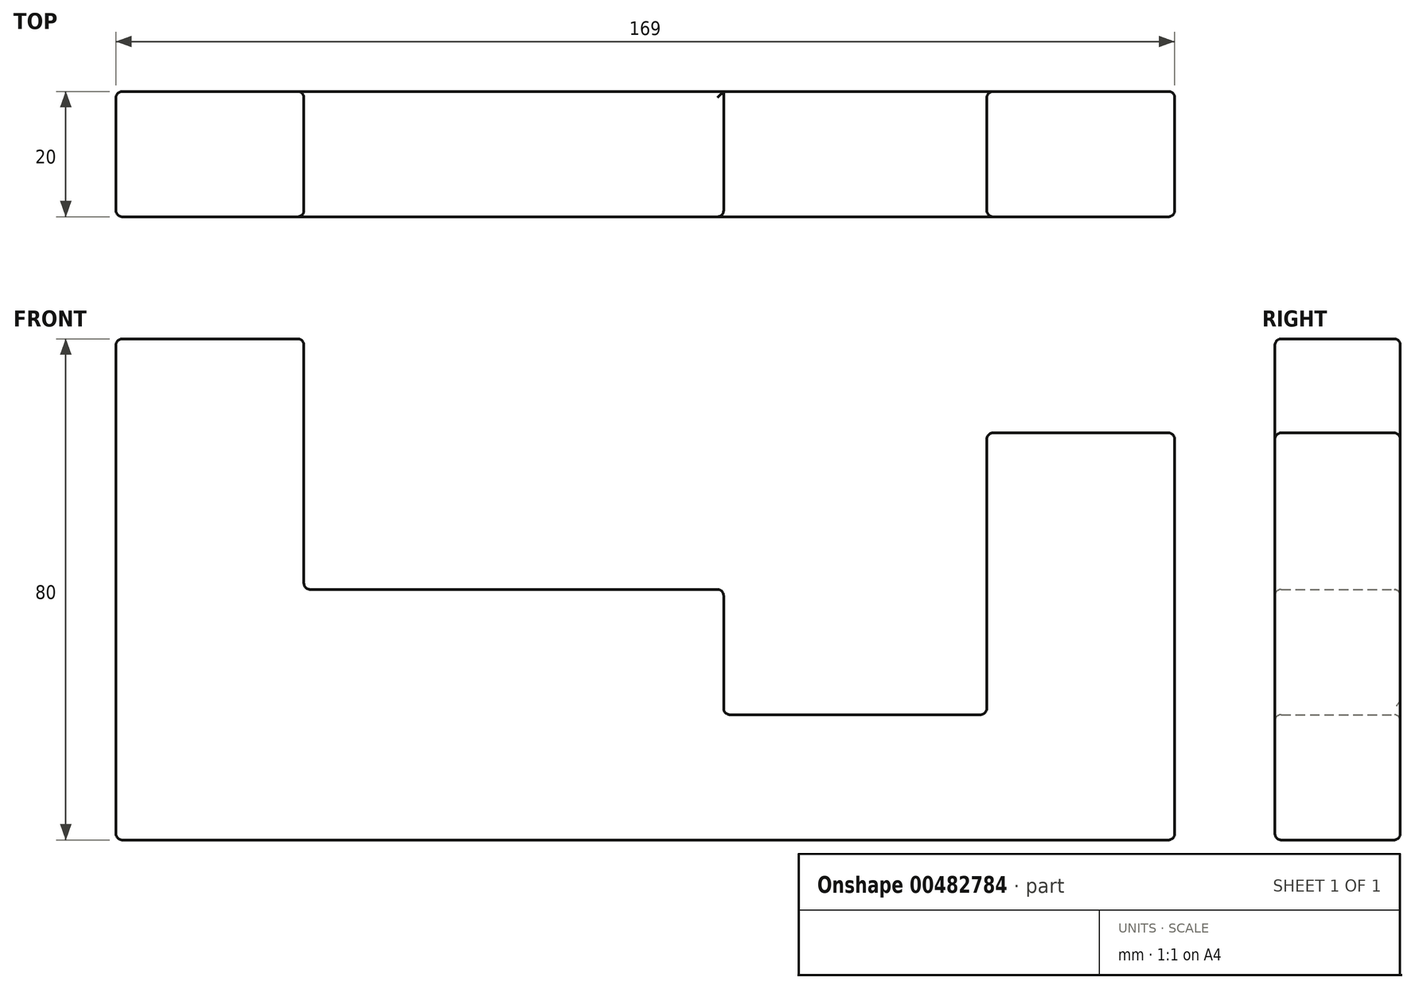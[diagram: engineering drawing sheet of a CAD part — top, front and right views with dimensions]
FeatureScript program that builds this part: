
annotation { "Feature Type Name" : "Feature", "Feature Type Description" : "" }
export const myFeature = defineFeature(function(context is Context, id is Id, definition is map)
    precondition{}
    {
        {
            var Q0;
            Q0=qCreatedBy(makeId("Front.planeOp"),FACE);
            var sketch = newSketch(context, id + "F0", { "sketchPlane" : qUnion([Q0])});
            skLineSegment(sketch, "E0", {"start": v(-54.8, -31.3) * mm, "end": v(114.2, -31.3) * mm});
            skLineSegment(sketch, "E1", {"start": v(-54.8, -31.3) * mm, "end": v(-54.8, 48.7) * mm});
            skLineSegment(sketch, "E2", {"start": v(-54.8, 48.7) * mm, "end": v(-24.8, 48.7) * mm});
            skLineSegment(sketch, "E3", {"start": v(-24.8, 48.7) * mm, "end": v(-24.8, 8.7) * mm});
            skLineSegment(sketch, "E4", {"start": v(-24.8, 8.7) * mm, "end": v(42.2, 8.7) * mm});
            skLineSegment(sketch, "E5", {"start": v(42.2, 8.7) * mm, "end": v(42.2, -11.3) * mm});
            skLineSegment(sketch, "E6", {"start": v(42.2, -11.3) * mm, "end": v(84.2, -11.3) * mm});
            skLineSegment(sketch, "E7", {"start": v(84.2, -11.3) * mm, "end": v(84.2, 33.7) * mm});
            skLineSegment(sketch, "E8", {"start": v(84.2, 33.7) * mm, "end": v(114.2, 33.7) * mm});
            skLineSegment(sketch, "E9", {"start": v(114.2, 33.7) * mm, "end": v(114.2, -31.3) * mm});
            skSolve(sketch);
        }
        {
            var Q0;
            Q0=makeQuery(id+"F0.imprint","IMPRINT",FACE,{"disambiguationData":[TD([[makeQuery(id+"F0.imprint","IMPRINT",EDGE,{"derivedFrom":sQuery(id+"F0.wireOp",EDGE,"E0")}),1.0]])]});
            extrude(context, id + "F1", {"entities" : qUnion([Q0]), "depth" : 20 * mm});
        }
        {
            var Q0;
            Q0=makeQuery(id+"F1.opExtrude","CAP_EDGE",EDGE,{"disambiguationData":[OSD([sQuery(id+"F0.wireOp",EDGE,"E2")])],"isStart":false});
            var Q1;
            Q1=makeQuery(id+"F1.opExtrude","CAP_EDGE",EDGE,{"disambiguationData":[OSD([sQuery(id+"F0.wireOp",EDGE,"E4")])],"isStart":false});
            var Q2;
            Q2=makeQuery(id+"F1.opExtrude","CAP_EDGE",EDGE,{"disambiguationData":[OSD([sQuery(id+"F0.wireOp",EDGE,"E3")])],"isStart":false});
            var Q3;
            Q3=makeQuery(id+"F1.opExtrude","CAP_EDGE",EDGE,{"disambiguationData":[OSD([sQuery(id+"F0.wireOp",EDGE,"E4")])],"isStart":true});
            var Q4;
            Q4=makeQuery(id+"F1.opExtrude","SWEPT_EDGE",EDGE,{"disambiguationData":[OSD([sQuery(id+"F0.wireOp",EDGE,"E2"),sQuery(id+"F0.wireOp",EDGE,"E3")])]});
            var Q5;
            Q5=makeQuery(id+"F1.opExtrude","SWEPT_FACE",FACE,{"disambiguationData":[OSD([sQuery(id+"F0.wireOp",EDGE,"E4")])]});
            var Q6;
            Q6=makeQuery(id+"F1.opExtrude","CAP_EDGE",EDGE,{"disambiguationData":[OSD([sQuery(id+"F0.wireOp",EDGE,"E5")])],"isStart":false});
            var Q7;
            Q7=makeQuery(id+"F1.opExtrude","SWEPT_FACE",FACE,{"disambiguationData":[OSD([sQuery(id+"F0.wireOp",EDGE,"E6")])]});
            var Q8;
            Q8=makeQuery(id+"F1.opExtrude","SWEPT_EDGE",EDGE,{"disambiguationData":[OSD([sQuery(id+"F0.wireOp",EDGE,"E8"),sQuery(id+"F0.wireOp",EDGE,"E9")])]});
            var Q9;
            Q9=makeQuery(id+"F1.opExtrude","CAP_EDGE",EDGE,{"disambiguationData":[OSD([sQuery(id+"F0.wireOp",EDGE,"E9")])],"isStart":true});
            var Q10;
            Q10=makeQuery(id+"F1.opExtrude","CAP_EDGE",EDGE,{"disambiguationData":[OSD([sQuery(id+"F0.wireOp",EDGE,"E8")])],"isStart":true});
            var Q11;
            Q11=makeQuery(id+"F1.opExtrude","CAP_EDGE",EDGE,{"disambiguationData":[OSD([sQuery(id+"F0.wireOp",EDGE,"E7")])],"isStart":true});
            var Q12;
            Q12=makeQuery(id+"F1.opExtrude","CAP_EDGE",EDGE,{"disambiguationData":[OSD([sQuery(id+"F0.wireOp",EDGE,"E1")])],"isStart":true});
            var Q13;
            Q13=makeQuery(id+"F1.opExtrude","CAP_EDGE",EDGE,{"disambiguationData":[OSD([sQuery(id+"F0.wireOp",EDGE,"E0")])],"isStart":true});
            var Q14;
            Q14=makeQuery(id+"F1.opExtrude","SWEPT_EDGE",EDGE,{"disambiguationData":[OSD([sQuery(id+"F0.wireOp",EDGE,"E0"),sQuery(id+"F0.wireOp",EDGE,"E1")])]});
            var Q15;
            Q15=makeQuery(id+"F1.opExtrude","SWEPT_EDGE",EDGE,{"disambiguationData":[OSD([sQuery(id+"F0.wireOp",EDGE,"E7"),sQuery(id+"F0.wireOp",EDGE,"E8")])]});
            var Q16;
            Q16=makeQuery(id+"F1.opExtrude","CAP_EDGE",EDGE,{"disambiguationData":[OSD([sQuery(id+"F0.wireOp",EDGE,"E3")])],"isStart":true});
            var Q17;
            Q17=makeQuery(id+"F1.opExtrude","CAP_EDGE",EDGE,{"disambiguationData":[OSD([sQuery(id+"F0.wireOp",EDGE,"E2")])],"isStart":true});
            var Q18;
            Q18=makeQuery(id+"F1.opExtrude","SWEPT_EDGE",EDGE,{"disambiguationData":[OSD([sQuery(id+"F0.wireOp",EDGE,"E0"),sQuery(id+"F0.wireOp",EDGE,"E9")])]});
            var Q19;
            Q19=makeQuery(id+"F1.opExtrude","SWEPT_EDGE",EDGE,{"disambiguationData":[OSD([sQuery(id+"F0.wireOp",EDGE,"E1"),sQuery(id+"F0.wireOp",EDGE,"E2")])]});
            fillet(context, id + "F2", {"entities" : qUnion([Q0, Q1, Q2, Q3, Q4, Q5, Q6, Q7, Q8, Q9, Q10, Q11, Q12, Q13, Q14, Q15, Q16, Q17, Q18, Q19]), "radius" : 1 * mm, "tangentPropagation" : true, "allowEdgeOverflow" : false});
        }
        {
            var Q0;
            Q0=makeQuery(id+"F1.opExtrude","CAP_EDGE",EDGE,{"disambiguationData":[OSD([sQuery(id+"F0.wireOp",EDGE,"E9")])],"isStart":false});
            fillet(context, id + "F3", {"entities" : qUnion([Q0]), "radius" : 1 * mm, "tangentPropagation" : true, "allowEdgeOverflow" : false});
        }
    });
